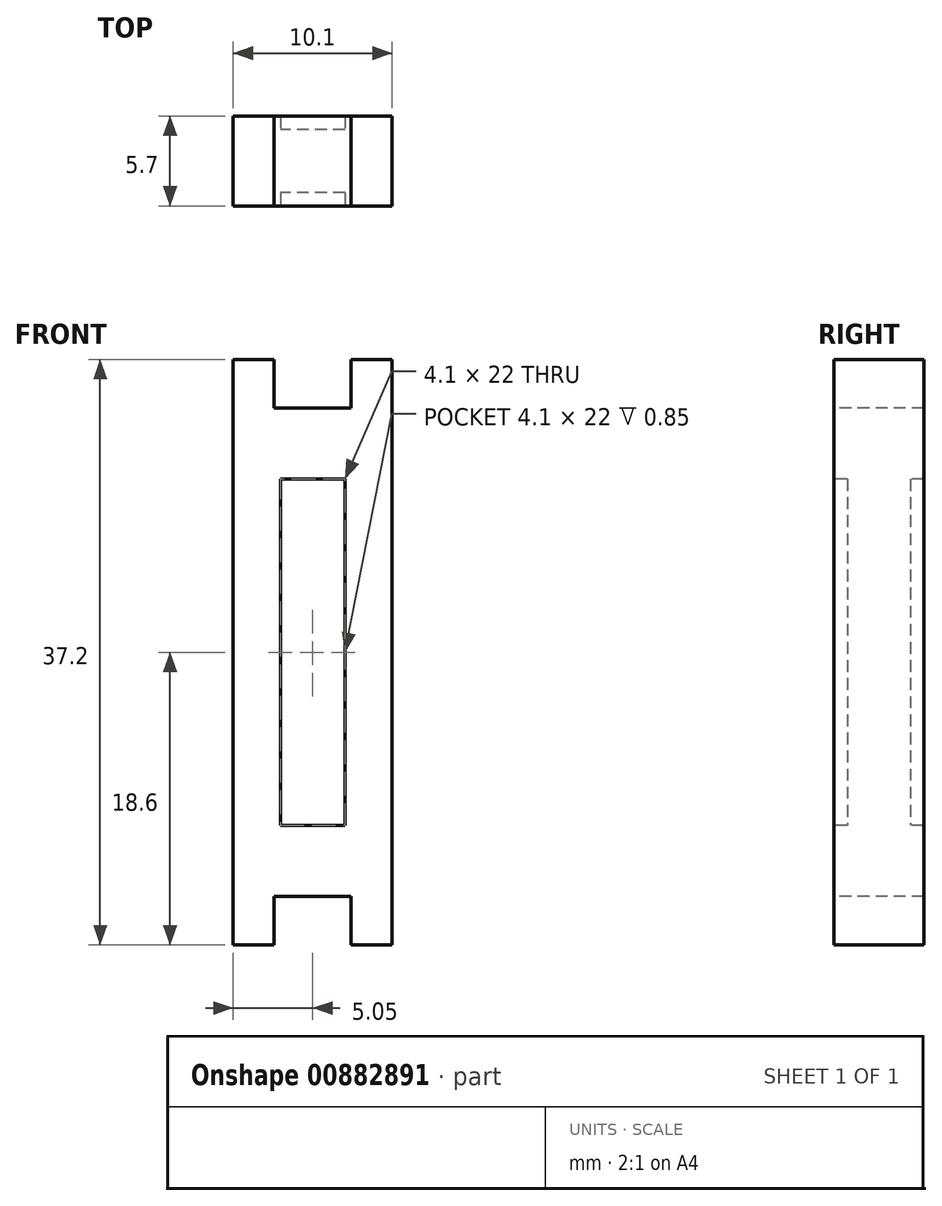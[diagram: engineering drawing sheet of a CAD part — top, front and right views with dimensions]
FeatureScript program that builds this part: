
annotation { "Feature Type Name" : "Feature", "Feature Type Description" : "" }
export const myFeature = defineFeature(function(context is Context, id is Id, definition is map)
    precondition{}
    {
        {
            var Q0;
            Q0=qCreatedBy(makeId("Front.planeOp"),FACE);
            var sketch = newSketch(context, id + "F0", { "sketchPlane" : qUnion([Q0])});
            skLineSegment(sketch, "E0", {"start": v(-5.05, -18.6) * mm, "end": v(-5.05, 18.6) * mm});
            skLineSegment(sketch, "E1", {"start": v(-5.05, 18.6) * mm, "end": v(-2.45, 18.6) * mm});
            skLineSegment(sketch, "E2", {"start": v(-2.45, 18.6) * mm, "end": v(-2.45, 15.5) * mm});
            skLineSegment(sketch, "E3", {"start": v(-2.45, 15.5) * mm, "end": v(2.45, 15.5) * mm});
            skLineSegment(sketch, "E4", {"start": v(2.45, 15.5) * mm, "end": v(2.45, 18.6) * mm});
            skLineSegment(sketch, "E5", {"start": v(2.45, 18.6) * mm, "end": v(5.05, 18.6) * mm});
            skLineSegment(sketch, "E6", {"start": v(5.05, 18.6) * mm, "end": v(5.05, -18.6) * mm});
            skLineSegment(sketch, "E7", {"start": v(5.05, -18.6) * mm, "end": v(2.45, -18.6) * mm});
            skLineSegment(sketch, "E8", {"start": v(2.45, -18.6) * mm, "end": v(2.45, -15.5) * mm});
            skLineSegment(sketch, "E9", {"start": v(2.45, -15.5) * mm, "end": v(-2.45, -15.5) * mm});
            skLineSegment(sketch, "E10", {"start": v(-2.45, -15.5) * mm, "end": v(-2.45, -18.6) * mm});
            skLineSegment(sketch, "E11", {"start": v(-2.45, -18.6) * mm, "end": v(-5.05, -18.6) * mm});
            skLineSegment(sketch, "E12", {"start": v(-2.05, 11) * mm, "end": v(-2.05, -11) * mm});
            skLineSegment(sketch, "E13", {"start": v(-2.05, -11) * mm, "end": v(2.05, -11) * mm});
            skLineSegment(sketch, "E14", {"start": v(2.05, -11) * mm, "end": v(2.05, 11) * mm});
            skLineSegment(sketch, "E15", {"start": v(2.05, 11) * mm, "end": v(-2.05, 11) * mm});
            skLineSegment(sketch, "E16", {"start": v(0, 0) * mm, "end": v(0, -47.94) * mm, "construction": true});
            skLineSegment(sketch, "E17", {"start": v(0, -47.94) * mm, "end": v(0, 38.26) * mm, "construction": true});
            skLineSegment(sketch, "E18", {"start": v(0, 38.26) * mm, "end": v(0, 0) * mm, "construction": true});
            skLineSegment(sketch, "E19", {"start": v(-70.84, 0) * mm, "end": v(0, 0) * mm, "construction": true});
            skLineSegment(sketch, "E20", {"start": v(65.45, 0) * mm, "end": v(0, 0) * mm, "construction": true});
            skSolve(sketch);
        }
        {
            var Q0;
            Q0=makeQuery(id+"F0.imprint","IMPRINT",FACE,{"disambiguationData":[TD([[makeQuery(id+"F0.imprint","IMPRINT",EDGE,{"derivedFrom":sQuery(id+"F0.wireOp",EDGE,"E0")}),-1.0]])]});
            extrude(context, id + "F1", {"entities" : qUnion([Q0]), "endBound" : BoundingType.SYMMETRIC, "oppositeDirection" : true, "depth" : 5.7 * mm, "offsetDistance" : 25 * mm});
        }
        {
            var Q0;
            Q0=makeQuery(id+"F0.imprint","IMPRINT",FACE,{"disambiguationData":[TD([[makeQuery(id+"F0.imprint","IMPRINT",EDGE,{"derivedFrom":sQuery(id+"F0.wireOp",EDGE,"E12")}),1.0]])]});
            extrude(context, id + "F2", {"entities" : qUnion([Q0]), "operationType" : NewBodyOperationType.ADD, "endBound" : BoundingType.SYMMETRIC, "depth" : 4 * mm, "offsetDistance" : 25 * mm});
        }
    });
